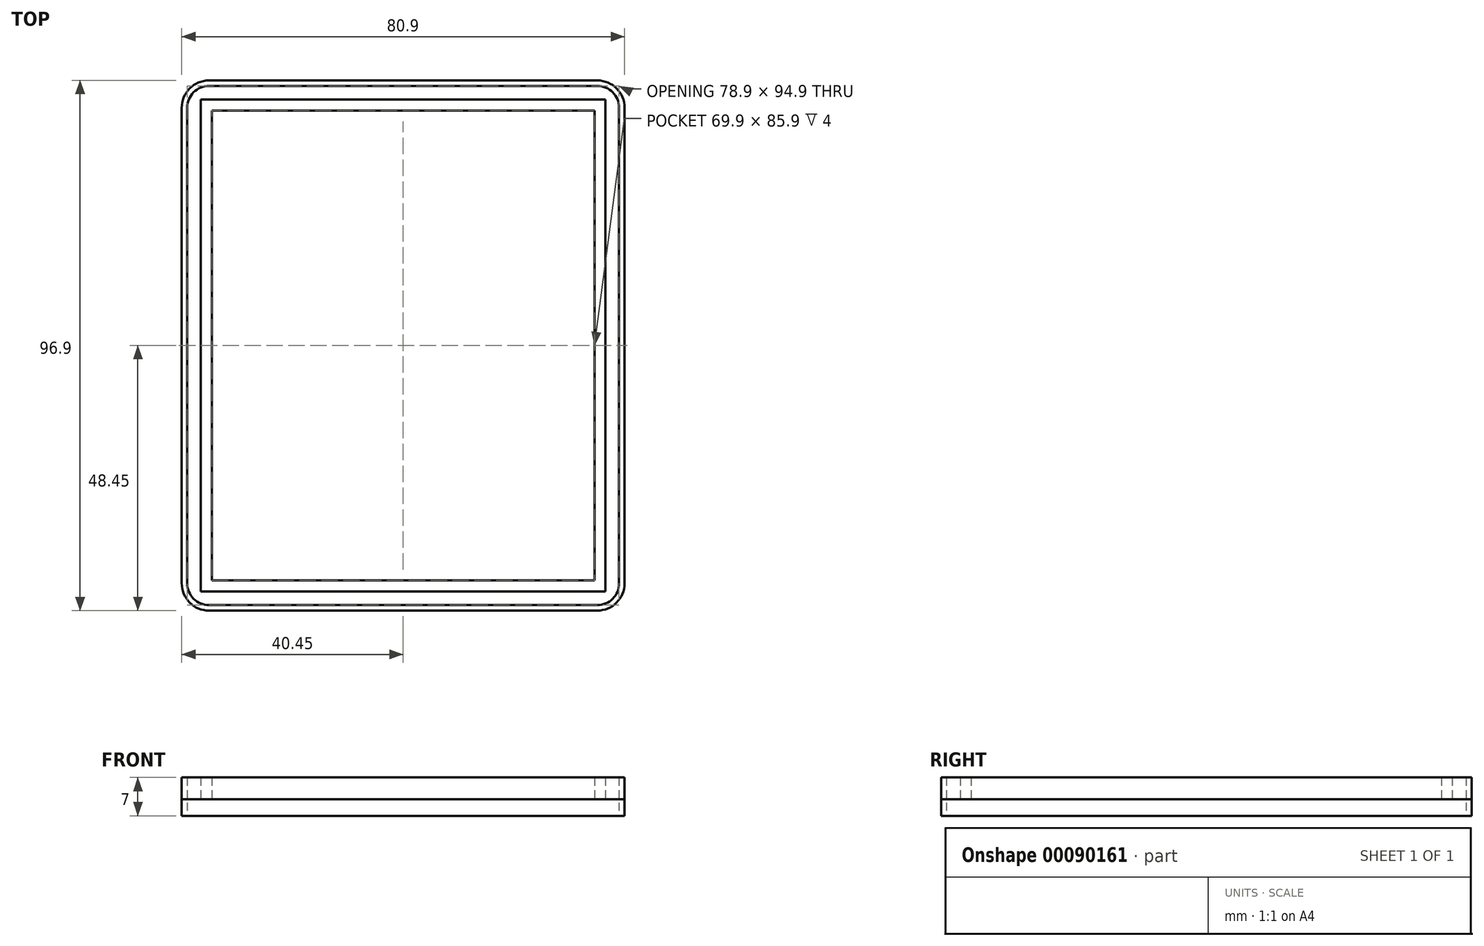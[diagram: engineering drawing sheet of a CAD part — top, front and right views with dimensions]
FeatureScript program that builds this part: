
annotation { "Feature Type Name" : "Feature", "Feature Type Description" : "" }
export const myFeature = defineFeature(function(context is Context, id is Id, definition is map)
    precondition{}
    {
        {
            var Q0;
            Q0=qCreatedBy(makeId("Top.planeOp"),FACE);
            var sketch = newSketch(context, id + "F0", { "sketchPlane" : qUnion([Q0])});
            skArc(sketch, "E0.0", {"start": v(-35.45, 47.45) * mm, "mid": v(-38.28, 46.28) * mm, "end": v(-39.45, 43.45) * mm});
            skLineSegment(sketch, "E0.1", {"start": v(-35.45, 47.45) * mm, "end": v(35.45, 47.45) * mm});
            skArc(sketch, "E0.6", {"start": v(39.45, 43.45) * mm, "mid": v(38.28, 46.28) * mm, "end": v(35.45, 47.45) * mm});
            skLineSegment(sketch, "E0.7", {"start": v(39.45, 43.45) * mm, "end": v(39.45, -43.45) * mm});
            skArc(sketch, "E0.8", {"start": v(35.45, -47.45) * mm, "mid": v(38.28, -46.28) * mm, "end": v(39.45, -43.45) * mm});
            skLineSegment(sketch, "E0.9", {"start": v(-35.45, -47.45) * mm, "end": v(35.45, -47.45) * mm});
            skLineSegment(sketch, "E0.10", {"start": v(-39.45, 43.45) * mm, "end": v(-39.45, -43.45) * mm});
            skArc(sketch, "E0.11", {"start": v(-39.45, -43.45) * mm, "mid": v(-38.28, -46.28) * mm, "end": v(-35.45, -47.45) * mm});
            skLineSegment(sketch, "E1.0", {"start": v(40.45, 43.45) * mm, "end": v(40.45, -43.45) * mm});
            skArc(sketch, "E1.1", {"start": v(35.45, -48.45) * mm, "mid": v(38.99, -46.99) * mm, "end": v(40.45, -43.45) * mm});
            skArc(sketch, "E1.2", {"start": v(40.45, 43.45) * mm, "mid": v(38.99, 46.99) * mm, "end": v(35.45, 48.45) * mm});
            skLineSegment(sketch, "E1.3", {"start": v(-35.45, -48.45) * mm, "end": v(35.45, -48.45) * mm});
            skLineSegment(sketch, "E1.4", {"start": v(-35.45, 48.45) * mm, "end": v(35.45, 48.45) * mm});
            skArc(sketch, "E1.5", {"start": v(-35.45, 48.45) * mm, "mid": v(-38.99, 46.99) * mm, "end": v(-40.45, 43.45) * mm});
            skLineSegment(sketch, "E1.6", {"start": v(-40.45, 43.45) * mm, "end": v(-40.45, -43.45) * mm});
            skArc(sketch, "E1.7", {"start": v(-40.45, -43.45) * mm, "mid": v(-38.99, -46.99) * mm, "end": v(-35.45, -48.45) * mm});
            skLineSegment(sketch, "E2.bottom", {"start": v(-34.95, 42.95) * mm, "end": v(34.95, 42.95) * mm});
            skLineSegment(sketch, "E2.top", {"start": v(-34.95, -42.95) * mm, "end": v(34.95, -42.95) * mm});
            skLineSegment(sketch, "E2.left", {"start": v(-34.95, 42.95) * mm, "end": v(-34.95, -42.95) * mm});
            skLineSegment(sketch, "E2.right", {"start": v(34.95, 42.95) * mm, "end": v(34.95, -42.95) * mm});
            skPoint(sketch, "E2.middle", {"position": v(0, 0) * mm});
            skLineSegment(sketch, "E3.0", {"start": v(-36.95, 44.95) * mm, "end": v(36.95, 44.95) * mm});
            skLineSegment(sketch, "E3.1", {"start": v(-36.95, 44.95) * mm, "end": v(-36.95, -44.95) * mm});
            skLineSegment(sketch, "E3.2", {"start": v(-36.95, -44.95) * mm, "end": v(36.95, -44.95) * mm});
            skLineSegment(sketch, "E3.3", {"start": v(36.95, 44.95) * mm, "end": v(36.95, -44.95) * mm});
            skLineSegment(sketch, "E4", {"start": v(-35.45, 43.45) * mm, "end": v(-35.45, -43.45) * mm, "construction": true});
            skLineSegment(sketch, "E5", {"start": v(35.45, -43.45) * mm, "end": v(-35.45, -43.45) * mm, "construction": true});
            skLineSegment(sketch, "E6", {"start": v(35.45, -43.45) * mm, "end": v(35.45, 43.45) * mm, "construction": true});
            skLineSegment(sketch, "E7", {"start": v(35.45, 43.45) * mm, "end": v(-35.45, 43.45) * mm, "construction": true});
            skSolve(sketch);
        }
        {
            var Q0;
            Q0=makeQuery(id+"F0.imprint","IMPRINT",FACE,{"disambiguationData":[TD([[makeQuery(id+"F0.imprint","IMPRINT",EDGE,{"derivedFrom":sQuery(id+"F0.wireOp",EDGE,"E0.0")}),-1.0]])]});
            var Q1;
            Q1=makeQuery(id+"F0.imprint","IMPRINT",FACE,{"disambiguationData":[TD([[makeQuery(id+"F0.imprint","IMPRINT",EDGE,{"derivedFrom":sQuery(id+"F0.wireOp",EDGE,"E0.0")}),1.0]])]});
            var Q2;
            Q2=makeQuery(id+"F0.imprint","IMPRINT",FACE,{"disambiguationData":[TD([[makeQuery(id+"F0.imprint","IMPRINT",EDGE,{"derivedFrom":sQuery(id+"F0.wireOp",EDGE,"E2.bottom")}),-1.0]])]});
            var Q3;
            Q3=makeQuery(id+"F0.imprint","IMPRINT",FACE,{"disambiguationData":[TD([[makeQuery(id+"F0.imprint","IMPRINT",EDGE,{"derivedFrom":sQuery(id+"F0.wireOp",EDGE,"E2.bottom")}),1.0]])]});
            extrude(context, id + "F1", {"entities" : qUnion([Q0, Q1, Q2, Q3]), "depth" : 3 * mm});
        }
        {
            var Q0;
            Q0=makeQuery(id+"F0.imprint","IMPRINT",FACE,{"disambiguationData":[TD([[makeQuery(id+"F0.imprint","IMPRINT",EDGE,{"derivedFrom":sQuery(id+"F0.wireOp",EDGE,"E0.0")}),-1.0]])]});
            extrude(context, id + "F2", {"entities" : qUnion([Q0]), "depth" : 7 * mm});
        }
        {
            var Q0;
            Q0=makeQuery(id+"F0.imprint","IMPRINT",FACE,{"disambiguationData":[TD([[makeQuery(id+"F0.imprint","IMPRINT",EDGE,{"derivedFrom":sQuery(id+"F0.wireOp",EDGE,"E2.bottom")}),1.0]])]});
            extrude(context, id + "F3", {"entities" : qUnion([Q0]), "operationType" : NewBodyOperationType.ADD, "depth" : 7 * mm});
        }
    });
